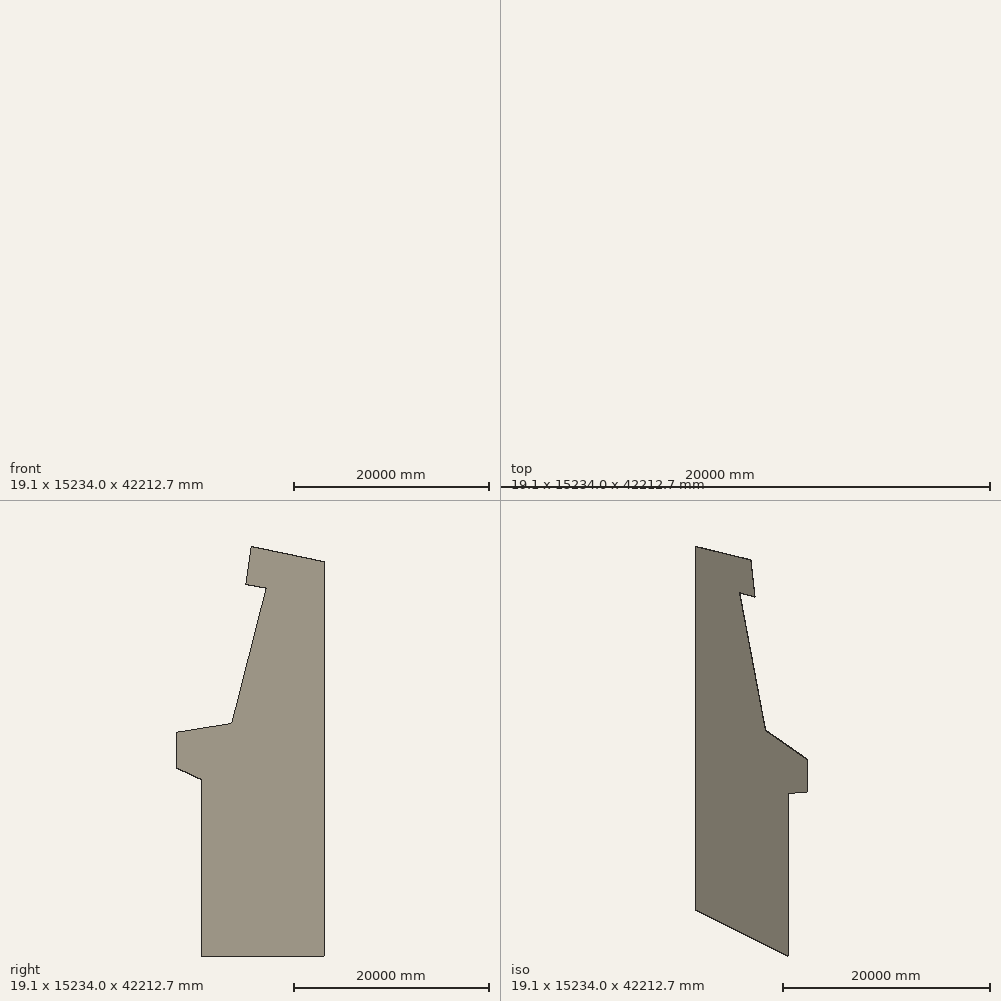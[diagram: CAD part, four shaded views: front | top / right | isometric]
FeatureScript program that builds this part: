
annotation { "Feature Type Name" : "Feature", "Feature Type Description" : "" }
export const myFeature = defineFeature(function(context is Context, id is Id, definition is map)
    precondition{}
    {
        {
            var Q0;
            Q0=qCreatedBy(makeId("Right.planeOp"),FACE);
            var sketch = newSketch(context, id + "F0", { "sketchPlane" : qUnion([Q0])});
            skLineSegment(sketch, "E0", {"start": v(-5661.93, -44278.65) * mm, "end": v(-5661.93, -26053.48) * mm});
            skLineSegment(sketch, "E1", {"start": v(7038.07, -44278.65) * mm, "end": v(7038.07, -3638.65) * mm});
            skLineSegment(sketch, "E2", {"start": v(7038.07, -3638.65) * mm, "end": v(-288.67, -2108.94) * mm});
            skLineSegment(sketch, "E3", {"start": v(1049.6, -6355.65) * mm, "end": v(-2503.76, -20286.2) * mm});
            skLineSegment(sketch, "E4", {"start": v(-1054.6, -5980.3) * mm, "end": v(-494.6, -2065.95) * mm});
            skLineSegment(sketch, "E5", {"start": v(-5661.93, -26053.48) * mm, "end": v(-7487.98, -25201.89) * mm});
            skLineSegment(sketch, "E6", {"start": v(-7487.98, -25201.89) * mm, "end": v(-7894.38, -25012.36) * mm});
            skLineSegment(sketch, "E7", {"start": v(-288.67, -2108.94) * mm, "end": v(-494.6, -2065.95) * mm});
            skLineSegment(sketch, "E8", {"start": v(-7894.38, -25012.36) * mm, "end": v(-7945.18, -24988.67) * mm});
            skLineSegment(sketch, "E9", {"start": v(7038.07, -44278.65) * mm, "end": v(-5661.93, -44278.65) * mm});
            skLineSegment(sketch, "E10", {"start": v(-7945.18, -21165.72) * mm, "end": v(-2503.76, -20286.2) * mm});
            skLineSegment(sketch, "E11", {"start": v(1049.6, -6355.65) * mm, "end": v(-1054.6, -5980.3) * mm});
            skLineSegment(sketch, "E12", {"start": v(-7945.18, -21165.72) * mm, "end": v(-8195.92, -21206.25) * mm});
            skLineSegment(sketch, "E13", {"start": v(-8195.92, -21206.25) * mm, "end": v(-8195.92, -24871.73) * mm});
            skLineSegment(sketch, "E14", {"start": v(-8195.92, -24871.73) * mm, "end": v(-7945.18, -24988.67) * mm});
            skSolve(sketch);
        }
        {
            var Q0;
            Q0=makeQuery(id+"F0.imprint","IMPRINT",FACE,{"disambiguationData":[TD([[makeQuery(id+"F0.imprint","IMPRINT",EDGE,{"derivedFrom":sQuery(id+"F0.wireOp",EDGE,"E0")}),-1.0]])]});
            extrude(context, id + "F1", {"entities" : qUnion([Q0]), "depth" : 19.05 * mm, "offsetDistance" : 25.4 * mm});
        }
    });
